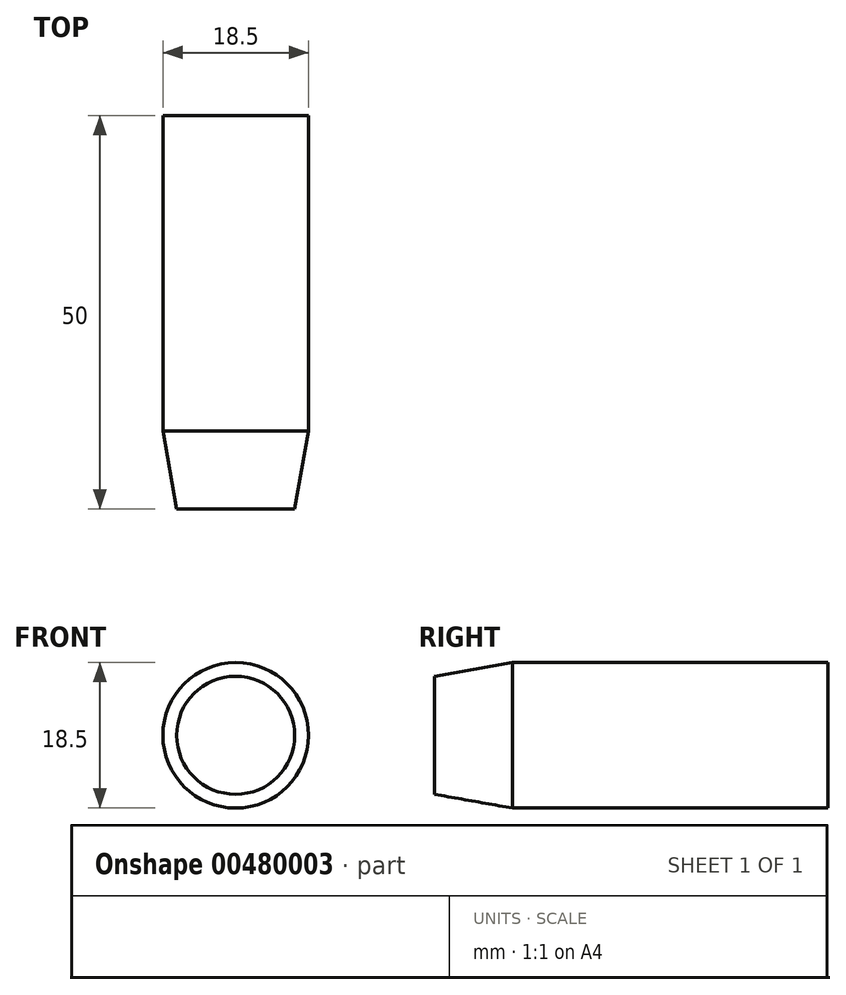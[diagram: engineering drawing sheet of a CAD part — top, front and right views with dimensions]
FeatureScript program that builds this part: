
annotation { "Feature Type Name" : "Feature", "Feature Type Description" : "" }
export const myFeature = defineFeature(function(context is Context, id is Id, definition is map)
    precondition{}
    {
        {
            var Q0;
            Q0=qCreatedBy(makeId("Front.planeOp"),FACE);
            var sketch = newSketch(context, id + "F0", { "sketchPlane" : qUnion([Q0])});
            skCircle(sketch, "E0", {"center": v(0, 0) * mm, "radius": 9.25 * mm});
            skSolve(sketch);
        }
        {
            var Q0;
            Q0=makeQuery(id+"F0.imprint","IMPRINT",FACE,{"disambiguationData":[TD([[makeQuery(id+"F0.imprint","IMPRINT",EDGE,{"derivedFrom":sQuery(id+"F0.wireOp",EDGE,"E0")}),1.0]])]});
            extrude(context, id + "F1", {"entities" : qUnion([Q0]), "depth" : 50 * mm});
        }
        {
            var Q0;
            Q0=makeQuery(id+"F1.opExtrude","CAP_EDGE",EDGE,{"disambiguationData":[OSD([sQuery(id+"F0.wireOp",EDGE,"E0")])],"isStart":false});
            chamfer(context, id + "F2", {"entities" : qUnion([Q0]), "chamferType" : ChamferType.OFFSET_ANGLE, "width" : 1.75 * mm, "oppositeDirection" : false, "angle" : 80 * degree, "tangentPropagation" : true});
        }
    });
